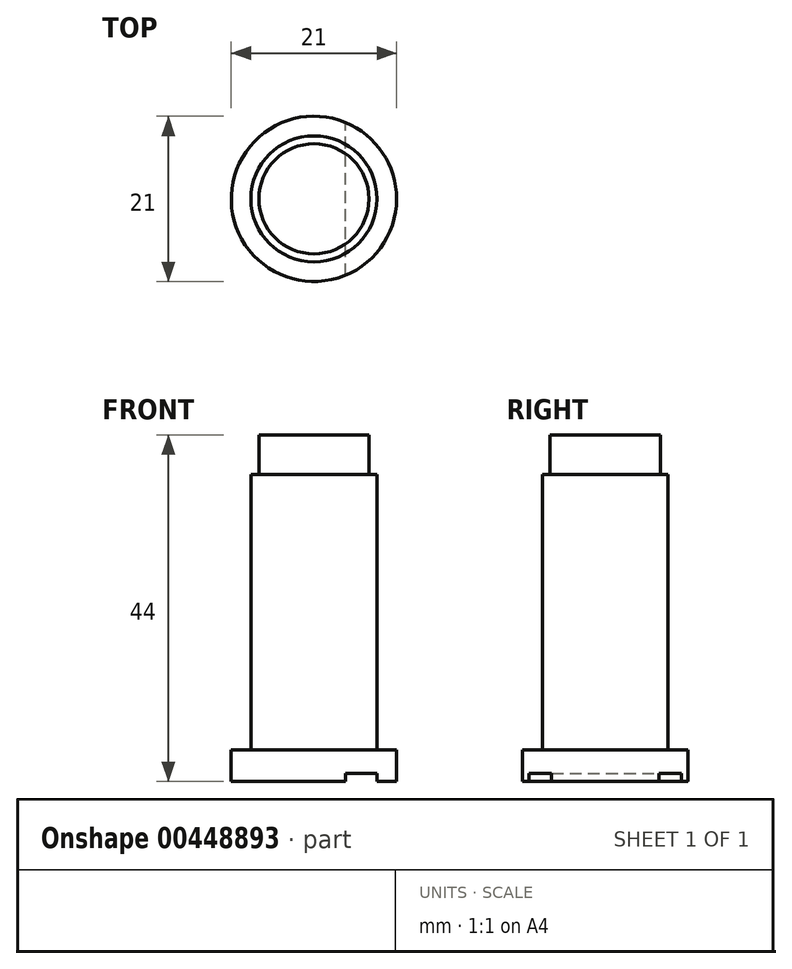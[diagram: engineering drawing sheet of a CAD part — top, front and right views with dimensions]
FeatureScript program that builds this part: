
annotation { "Feature Type Name" : "Feature", "Feature Type Description" : "" }
export const myFeature = defineFeature(function(context is Context, id is Id, definition is map)
    precondition{}
    {
        {
            var Q0;
            Q0=qCreatedBy(makeId("Top.planeOp"),FACE);
            var sketch = newSketch(context, id + "F0", { "sketchPlane" : qUnion([Q0])});
            skCircle(sketch, "E0", {"center": v(0, 0) * mm, "radius": 10.5 * mm});
            skSolve(sketch);
        }
        {
            var Q0;
            Q0=qSketchRegion(id+"F0",true);
            extrude(context, id + "F1", {"entities" : qUnion([Q0]), "depth" : 4 * mm});
        }
        {
            var Q0;
            Q0=qCreatedBy(makeId("Top.planeOp"),FACE);
            var sketch = newSketch(context, id + "F2", { "sketchPlane" : qUnion([Q0])});
            skCircle(sketch, "E1", {"center": v(0, 0) * mm, "radius": 8 * mm});
            skSolve(sketch);
        }
        {
            var Q0;
            Q0=qSketchRegion(id+"F2",true);
            extrude(context, id + "F3", {"entities" : qUnion([Q0]), "operationType" : NewBodyOperationType.ADD, "depth" : 39 * mm});
        }
        {
            var Q0;
            Q0=qCreatedBy(makeId("Right.planeOp"),FACE);
            var sketch = newSketch(context, id + "F4", { "sketchPlane" : qUnion([Q0])});
            skLineSegment(sketch, "E2", {"start": v(0, 44) * mm, "end": v(0, 39) * mm});
            skLineSegment(sketch, "E3", {"start": v(0, 39) * mm, "end": v(7, 39) * mm});
            skLineSegment(sketch, "E4", {"start": v(7, 39) * mm, "end": v(7, 44) * mm});
            skLineSegment(sketch, "E5", {"start": v(7, 44) * mm, "end": v(0, 44) * mm});
            skSolve(sketch);
        }
        {
            var Q0;
            Q0=makeQuery(id+"F4.imprint","IMPRINT",FACE,{"disambiguationData":[TD([[makeQuery(id+"F4.imprint","IMPRINT",EDGE,{"derivedFrom":sQuery(id+"F4.wireOp",EDGE,"E2")}),1.0]])]});
            var Q1;
            Q1=sQuery(id+"F4.wireOp",EDGE,"E2");
            revolve(context, id + "F5", {"operationType" : NewBodyOperationType.ADD, "entities" : qUnion([Q0]), "axis" : qUnion([Q1]), "revolveType" : RevolveType.FULL});
        }
        {
            var Q0;
            Q0=qCreatedBy(makeId("Top.planeOp"),FACE);
            var sketch = newSketch(context, id + "F6", { "sketchPlane" : qUnion([Q0])});
            skLineSegment(sketch, "E6.bottom", {"start": v(4, -11.48) * mm, "end": v(8, -11.48) * mm});
            skLineSegment(sketch, "E6.top", {"start": v(4, 13.5) * mm, "end": v(8, 13.5) * mm});
            skLineSegment(sketch, "E6.left", {"start": v(4, -11.48) * mm, "end": v(4, 13.5) * mm});
            skLineSegment(sketch, "E6.right", {"start": v(8, -11.48) * mm, "end": v(8, 13.5) * mm});
            skSolve(sketch);
        }
        {
            var Q0;
            Q0=qSketchRegion(id+"F6",true);
            extrude(context, id + "F7", {"entities" : qUnion([Q0]), "operationType" : NewBodyOperationType.REMOVE, "depth" : 1 * mm});
        }
    });
